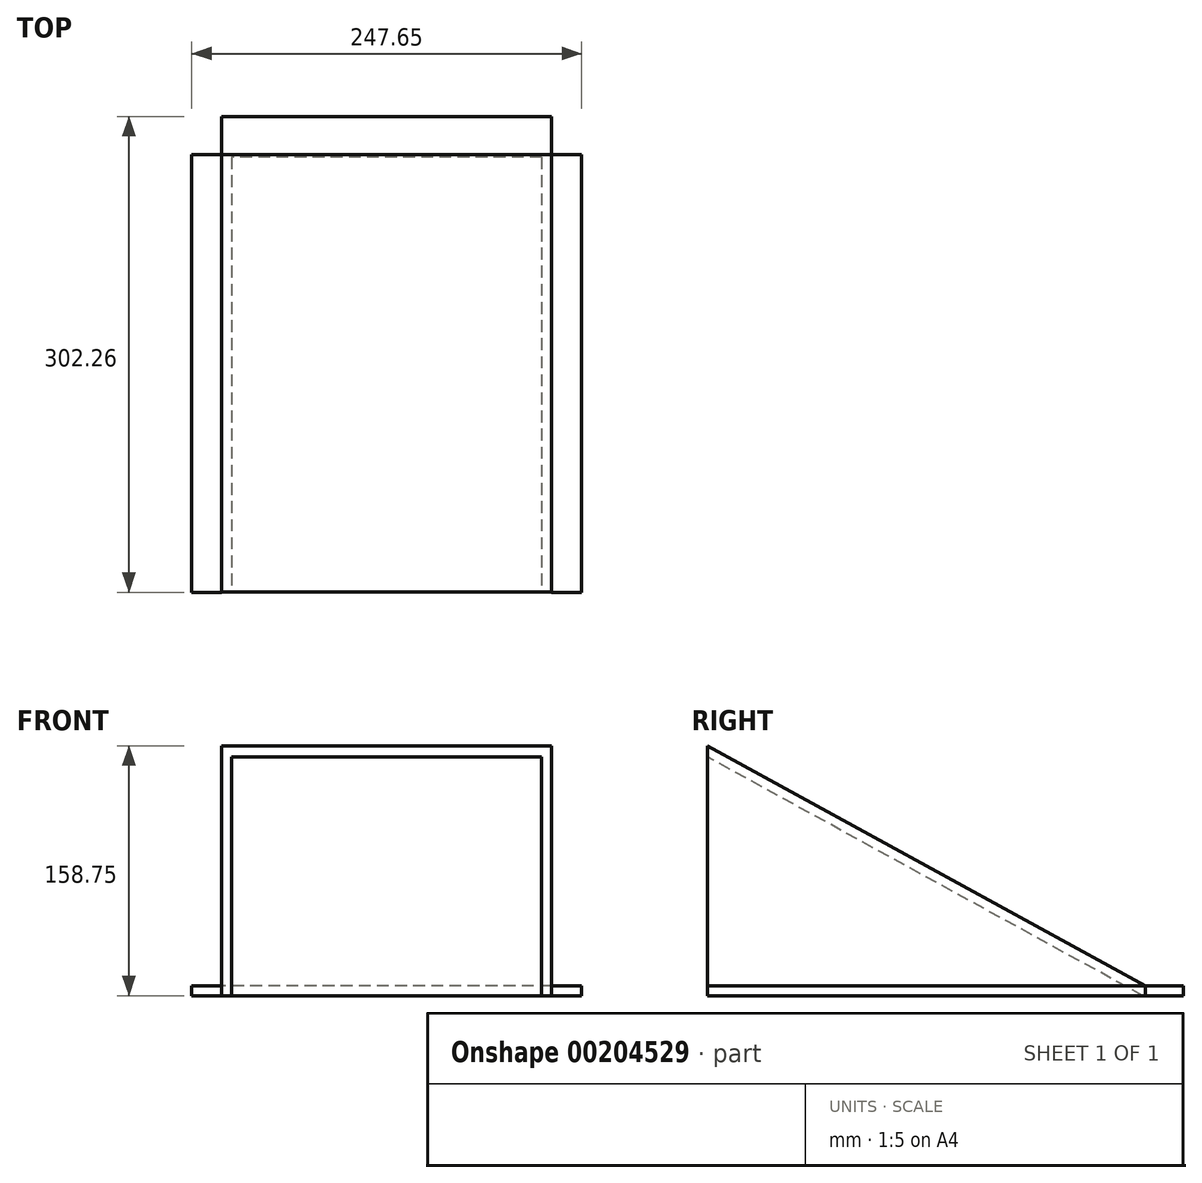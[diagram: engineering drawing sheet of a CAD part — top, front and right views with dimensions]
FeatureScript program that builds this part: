
annotation { "Feature Type Name" : "Feature", "Feature Type Description" : "" }
export const myFeature = defineFeature(function(context is Context, id is Id, definition is map)
    precondition{}
    {
        {
            var Q0;
            Q0=qCreatedBy(makeId("Right.planeOp"),FACE);
            var sketch = newSketch(context, id + "F0", { "sketchPlane" : qUnion([Q0])});
            skLineSegment(sketch, "E0", {"start": v(-11.58, 6.35) * mm, "end": v(-289.53, 158.75) * mm});
            skLineSegment(sketch, "E1", {"start": v(-289.53, 158.75) * mm, "end": v(-289.53, 0) * mm});
            skLineSegment(sketch, "E2", {"start": v(0, 0) * mm, "end": v(-289.53, 0) * mm});
            skLineSegment(sketch, "E3.0", {"start": v(-13.2, 0) * mm, "end": v(-289.53, 151.5) * mm});
            skLineSegment(sketch, "E4", {"start": v(0, 0) * mm, "end": v(0, 6.35) * mm});
            skLineSegment(sketch, "E5", {"start": v(0, 6.35) * mm, "end": v(-11.58, 6.35) * mm});
            skSolve(sketch);
        }
        {
            var Q0;
            {var subQ0=sQuery(id+"F0.wireOp",EDGE,"E0");Q0=makeQuery(id+"F0.imprint","IMPRINT",FACE,{"disambiguationData":[TD([[makeQuery(id+"F0.imprint","IMPRINT",EDGE,{"derivedFrom":subQ0}),1.0]])]});}
            extrude(context, id + "F1", {"entities" : qUnion([Q0]), "depth" : 203.2 * mm});
        }
        {
            var Q0;
            {var subQ3=sQuery(id+"F0.wireOp",EDGE,"E3.0");Q0=makeQuery(id+"F0.imprint","IMPRINT",FACE,{"disambiguationData":[TD([[makeQuery(id+"F0.imprint","IMPRINT",EDGE,{"derivedFrom":subQ3}),1.0]])]});}
            extrude(context, id + "F2", {"entities" : qUnion([Q0]), "operationType" : NewBodyOperationType.ADD, "depth" : 6.35 * mm});
        }
        {
            var Q0;
            Q0=makeQuery(id+"F1.opExtrude","CAP_FACE",FACE,{"disambiguationData":[OSD([sQuery(id+"F0.wireOp",EDGE,"E0"),sQuery(id+"F0.wireOp",EDGE,"E1"),sQuery(id+"F0.wireOp",EDGE,"E2"),sQuery(id+"F0.wireOp",EDGE,"E3.0")])],"isStart":false});
            var sketch = newSketch(context, id + "F3", { "sketchPlane" : qUnion([Q0])});
            skLineSegment(sketch, "E6", {"start": v(-289.53, 158.75) * mm, "end": v(-289.53, 0) * mm});
            skPoint(sketch, "E6.endSnap0", {"position": v(-289.53, 155.13) * mm});
            skLineSegment(sketch, "E7", {"start": v(-11.58, 6.35) * mm, "end": v(-289.53, 158.75) * mm});
            skLineSegment(sketch, "E8", {"start": v(-289.53, 0) * mm, "end": v(0, 0) * mm});
            skLineSegment(sketch, "E9", {"start": v(0, 0) * mm, "end": v(0, 6.35) * mm});
            skLineSegment(sketch, "E10", {"start": v(0, 6.35) * mm, "end": v(-11.58, 6.35) * mm});
            skSolve(sketch);
        }
        {
            var Q0;
            Q0 = qSketchRegion(id + "F3", true);
            extrude(context, id + "F4", {"entities" : qUnion([Q0]), "operationType" : NewBodyOperationType.ADD, "depth" : 6.35 * mm});
        }
        {
            var Q0;
            Q0=qCreatedBy(makeId("Top.planeOp"),FACE);
            var sketch = newSketch(context, id + "F5", { "sketchPlane" : qUnion([Q0])});
            skLineSegment(sketch, "E11", {"start": v(-19.05, -11.54) * mm, "end": v(-19.05, -289.56) * mm});
            skLineSegment(sketch, "E12", {"start": v(-19.05, -289.56) * mm, "end": v(0, -289.56) * mm});
            skLineSegment(sketch, "E13", {"start": v(0, -289.56) * mm, "end": v(0, -11.54) * mm});
            skLineSegment(sketch, "E14", {"start": v(0, 12.7) * mm, "end": v(209.55, 12.7) * mm});
            skLineSegment(sketch, "E15", {"start": v(209.55, 0) * mm, "end": v(0, 0) * mm});
            skLineSegment(sketch, "E16", {"start": v(228.6, -11.45) * mm, "end": v(228.6, -289.56) * mm});
            skLineSegment(sketch, "E17", {"start": v(228.6, -289.56) * mm, "end": v(209.55, -289.56) * mm});
            skLineSegment(sketch, "E18", {"start": v(209.55, -289.56) * mm, "end": v(209.55, -11.45) * mm});
            skLineSegment(sketch, "E19", {"start": v(0, 12.7) * mm, "end": v(0, 0) * mm});
            skLineSegment(sketch, "E20", {"start": v(209.55, 12.7) * mm, "end": v(209.55, 0) * mm});
            skLineSegment(sketch, "E21", {"start": v(0, -11.54) * mm, "end": v(-19.05, -11.54) * mm});
            skLineSegment(sketch, "E22", {"start": v(209.55, -11.45) * mm, "end": v(228.6, -11.45) * mm});
            skSolve(sketch);
        }
        {
            var Q0;
            Q0 = qSketchRegion(id + "F5", true);
            extrude(context, id + "F6", {"entities" : qUnion([Q0]), "operationType" : NewBodyOperationType.ADD, "depth" : 6.35 * mm});
        }
    });
